AUTODESK INVENTOR PART (.ipt)
format: ipt  version: 2022 (Build 260153000, 153)  size: 1,059,840 bytes
history: native  units: mm
features: extrude x2, sketch x2, fillet x1, pattern_circular x1
ambient origin geometry x8: Origin, YZ Plane, XZ Plane, XY Plane, X Axis, Y Axis, Z Axis, Center Point
bodies: Solid1 (feature_tree)
feature tree (6):
  extrude  "Extrusion1"  Depth=1.3mm
  extrude  "Extrusion3"  Depth=10.0mm TaperAngle=0.0deg
  fillet  "Fillet2"  Radius=660.0mm
  pattern_circular  "Circular Pattern2"  [2 undecoded]
  sketch  "Sketch1"  dims[d0=64.1mm d1=1.3mm]
  sketch  "Sketch3"  dims[d2=15.0mm d3=0.0mm d12=0.8mm d13=1.8mm d14=8.726646mm d15=0.523599mm d16=0.523599mm d17=0.523599mm d18=0.523599mm d19=0.523599mm d20=2.792527mm d21=0.523599mm d22=64.1mm d23=66.683194mm d24=1.677942mm d25=9.19019mm d26=7.512247mm d27=5.834305mm d28=4.156362mm d29=2.47842mm d30=0.523599mm d31=0.523599mm d32=0.523599mm d33=0.523599mm d34=0.523599mm d35=10.868132mm d36=12.546074mm d37=14.224017mm d38=15.901959mm d39=17.579902mm d40=0.523599mm d41=0.523599mm d42=19.257844mm d43=20.935786mm d44=0.224037mm d45=68.620589mm d46=10.0mm d47=0.0mm d48=660.0mm d49=360.0deg d51=0.65mm]
note: 2 required parameter values undecoded (feature->parameter linkage not recoverable at this tier; creation-order binding heuristic only, values carry confidence <= 0.55)
